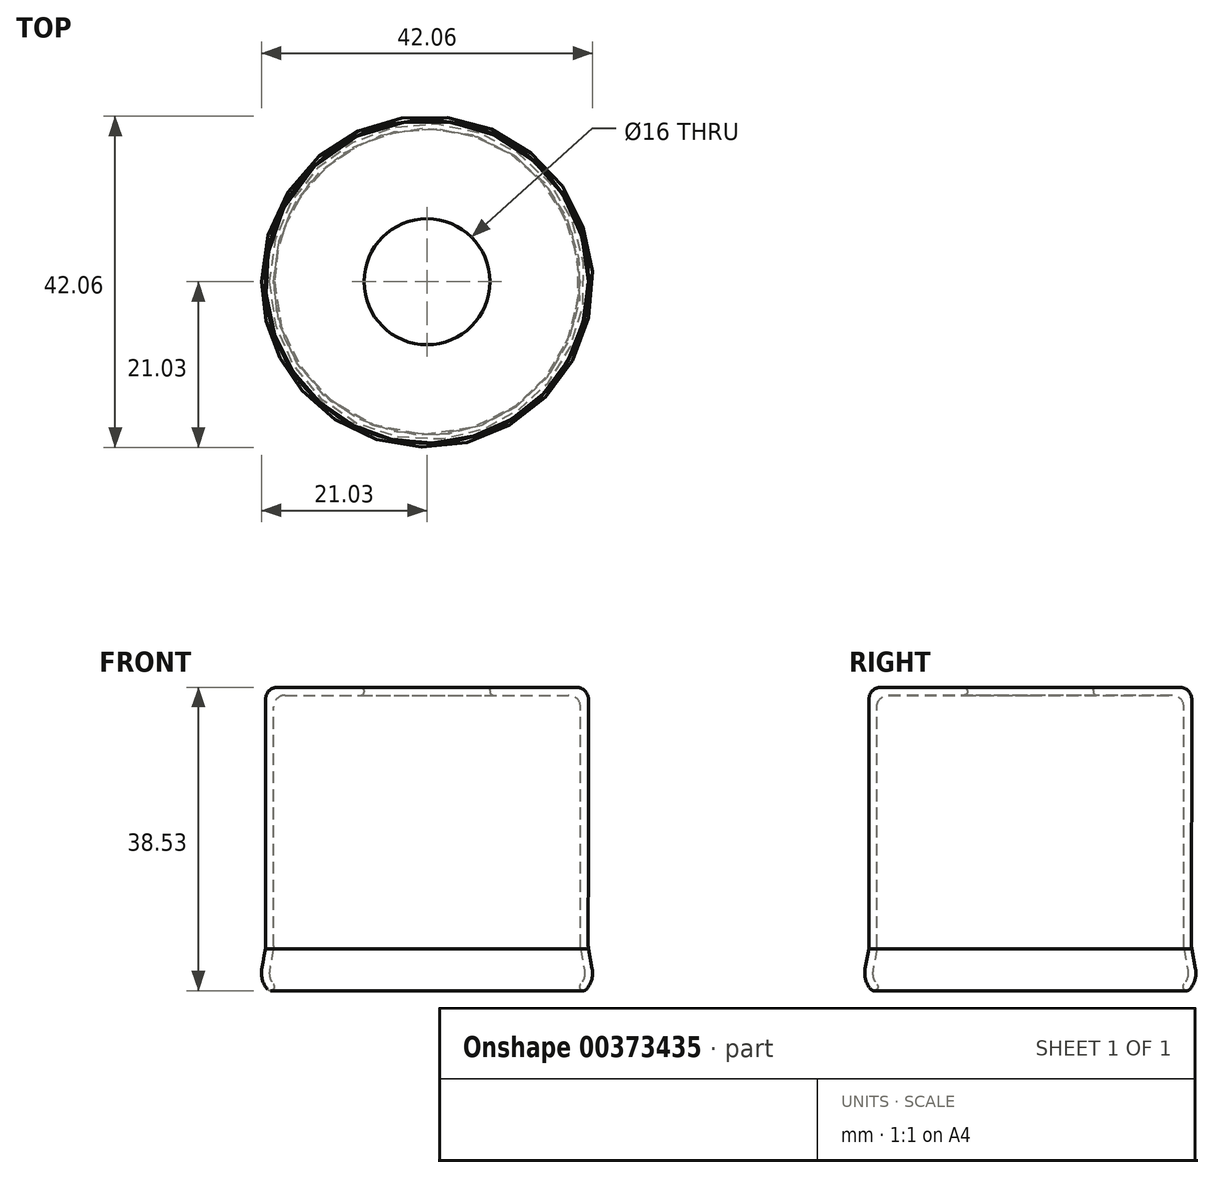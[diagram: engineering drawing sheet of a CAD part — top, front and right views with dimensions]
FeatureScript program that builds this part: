
annotation { "Feature Type Name" : "Feature", "Feature Type Description" : "" }
export const myFeature = defineFeature(function(context is Context, id is Id, definition is map)
    precondition{}
    {
        {
            var Q0;
            Q0=qCreatedBy(makeId("Front.planeOp"),FACE);
            var sketch = newSketch(context, id + "F0", { "sketchPlane" : qUnion([Q0])});
            skLineSegment(sketch, "E0", {"start": v(0, 0) * mm, "end": v(19.5, 0) * mm});
            skLineSegment(sketch, "E1", {"start": v(20, 1.75) * mm, "end": v(19.48, 4.7) * mm});
            skArc(sketch, "E2", {"start": v(19.5, 0) * mm, "mid": v(19.95, 0.82) * mm, "end": v(20, 1.75) * mm});
            skLineSegment(sketch, "E3", {"start": v(19.48, 4.7) * mm, "end": v(19.5, 36.7) * mm});
            skArc(sketch, "E4.1", {"start": v(20.24, -0.67) * mm, "mid": v(20.91, 0.54) * mm, "end": v(20.98, 1.92) * mm});
            skLineSegment(sketch, "E4.2", {"start": v(20.98, 1.92) * mm, "end": v(20.53, 4.48) * mm});
            skArc(sketch, "E5", {"start": v(19.5, 0) * mm, "mid": v(19.54, -0.7) * mm, "end": v(20.24, -0.67) * mm});
            skLineSegment(sketch, "E6", {"start": v(0, 0) * mm, "end": v(0, 49.5) * mm});
            skLineSegment(sketch, "E7", {"start": v(20.5, 36.7) * mm, "end": v(20.5, 37.7) * mm});
            skLineSegment(sketch, "E8.0", {"start": v(20.48, 4.7) * mm, "end": v(20.5, 36.7) * mm});
            skLineSegment(sketch, "E9", {"start": v(20.53, 4.48) * mm, "end": v(20.48, 4.7) * mm});
            skLineSegment(sketch, "E10", {"start": v(20.5, 37.7) * mm, "end": v(8.4, 37.7) * mm});
            skLineSegment(sketch, "E11", {"start": v(8, 37.3) * mm, "end": v(8, 37.1) * mm});
            skLineSegment(sketch, "E12", {"start": v(8.4, 36.7) * mm, "end": v(19.5, 36.7) * mm});
            skPoint(sketch, "E13.visualSharp", {"position": v(8, 37.7) * mm});
            skArc(sketch, "E13.filletArc", {"start": v(8.4, 37.7) * mm, "mid": v(8.12, 37.59) * mm, "end": v(8, 37.3) * mm});
            skPoint(sketch, "E14.visualSharp", {"position": v(8, 36.7) * mm});
            skArc(sketch, "E14.filletArc", {"start": v(8, 37.1) * mm, "mid": v(8.12, 36.82) * mm, "end": v(8.4, 36.7) * mm});
            skSolve(sketch);
        }
        {
            var Q0;
            {var subQ1=sQuery(id+"F0.wireOp",EDGE,"zRALZGh6-zfNs-TNwz-CvcH-FD8Cm7Anhlul");Q0=makeQuery(id+"F0.imprint","IMPRINT",FACE,{"disambiguationData":[TD([[makeQuery(id+"F0.imprint","IMPRINT",EDGE,{"derivedFrom":subQ1}),1.0]])]});}
            var Q1;
            {var subQ5=sQuery(id+"F0.wireOp",EDGE,"E1");Q1=makeQuery(id+"F0.imprint","IMPRINT",FACE,{"disambiguationData":[TD([[makeQuery(id+"F0.imprint","IMPRINT",EDGE,{"derivedFrom":subQ5}),-1.0]])]});}
            var Q2;
            Q2=sQuery(id+"F0.wireOp",EDGE,"E6");
            revolve(context, id + "F1", {"entities" : qUnion([Q0, Q1]), "axis" : qUnion([Q2]), "revolveType" : RevolveType.FULL});
        }
        {
            var Q0;
            Q0=makeQuery(id+"F1.opRevolve","SWEPT_EDGE",EDGE,{"disambiguationData":[OSD([sQuery(id+"F0.wireOp",EDGE,"E7"),sQuery(id+"F0.wireOp",EDGE,"E10")])]});
            var Q1;
            Q1=makeQuery(id+"F1.opRevolve","SWEPT_EDGE",EDGE,{"disambiguationData":[OSD([sQuery(id+"F0.wireOp",EDGE,"E3"),sQuery(id+"F0.wireOp",EDGE,"E12")])]});
            var Q2;
            Q2=makeQuery(id+"F1.opRevolve","SWEPT_EDGE",EDGE,{"disambiguationData":[OSD([sQuery(id+"F0.wireOp",EDGE,"E8.0"),sQuery(id+"F0.wireOp",EDGE,"E9")])]});
            var Q3;
            Q3=makeQuery(id+"F1.opRevolve","SWEPT_EDGE",EDGE,{"disambiguationData":[OSD([sQuery(id+"F0.wireOp",EDGE,"E1"),sQuery(id+"F0.wireOp",EDGE,"E3")])]});
            fillet(context, id + "F2", {"entities" : qUnion([Q0, Q1, Q2, Q3]), "radius" : 1.5 * mm, "tangentPropagation" : true, "allowEdgeOverflow" : false});
        }
    });
